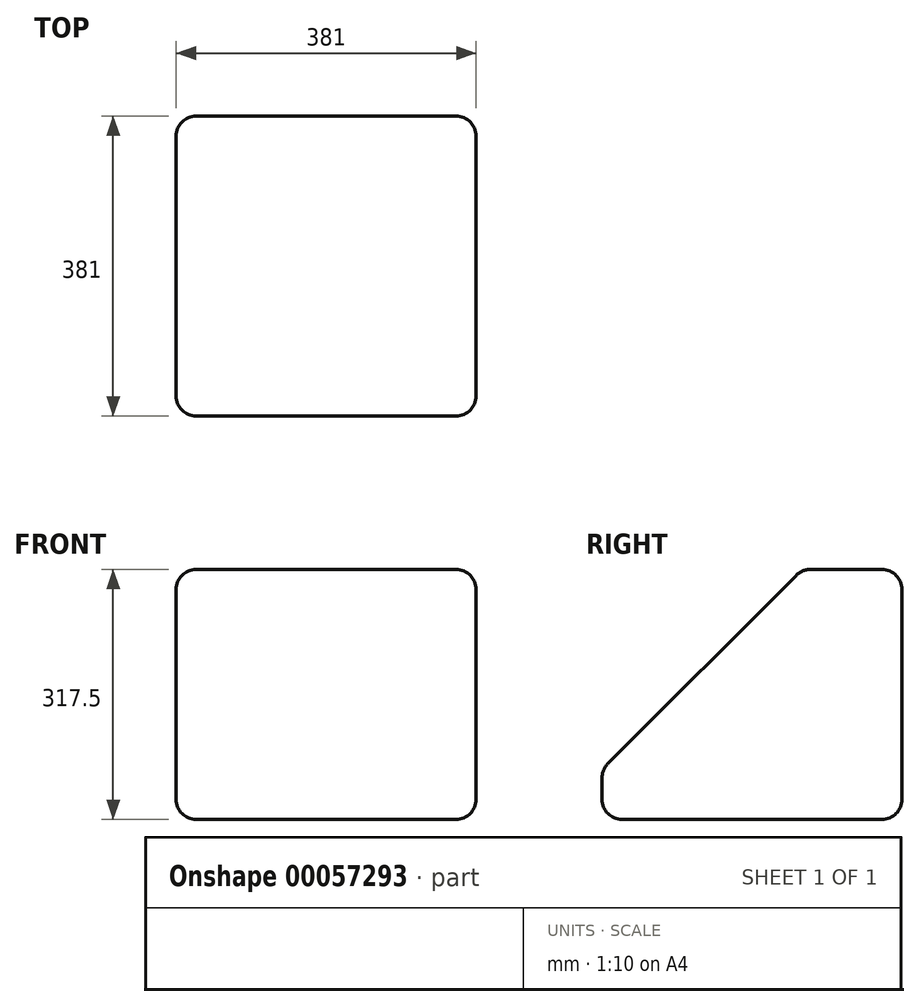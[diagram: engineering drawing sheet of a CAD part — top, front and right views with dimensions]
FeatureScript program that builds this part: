
annotation { "Feature Type Name" : "Feature", "Feature Type Description" : "" }
export const myFeature = defineFeature(function(context is Context, id is Id, definition is map)
    precondition{}
    {
        {
            var Q0;
            Q0=qCreatedBy(makeId("Top.planeOp"),FACE);
            var sketch = newSketch(context, id + "F0", { "sketchPlane" : qUnion([Q0])});
            skLineSegment(sketch, "E0.rect.bottom", {"start": v(190.5, -190.5) * mm, "end": v(-190.5, -190.5) * mm});
            skLineSegment(sketch, "E0.rect.top", {"start": v(190.5, 190.5) * mm, "end": v(-190.5, 190.5) * mm});
            skLineSegment(sketch, "E0.rect.left", {"start": v(190.5, -190.5) * mm, "end": v(190.5, 190.5) * mm});
            skLineSegment(sketch, "E0.rect.right", {"start": v(-190.5, -190.5) * mm, "end": v(-190.5, 190.5) * mm});
            skPoint(sketch, "E0.rect.middle", {"position": v(0, 0) * mm});
            skSolve(sketch);
        }
        {
            var Q0;
            Q0=makeQuery(id+"F0.imprint","IMPRINT",FACE,{"disambiguationData":[TD([[makeQuery(id+"F0.imprint","IMPRINT",EDGE,{"derivedFrom":sQuery(id+"F0.wireOp",EDGE,"E0.rect.bottom")}),-1.0]])]});
            extrude(context, id + "F1", {"entities" : qUnion([Q0]), "depth" : 317.5 * mm});
        }
        {
            var Q0;
            Q0=makeQuery(id+"F1.opExtrude","CAP_EDGE",EDGE,{"disambiguationData":[OSD([sQuery(id+"F0.wireOp",EDGE,"E0.rect.bottom")])],"isStart":false});
            chamfer(context, id + "F2", {"entities" : qUnion([Q0]), "width" : 254 * mm, "tangentPropagation" : true});
        }
        {
            var Q0;
            Q0=makeQuery(id+"F1.opExtrude","SWEPT_FACE",FACE,{"disambiguationData":[OSD([sQuery(id+"F0.wireOp",EDGE,"E0.rect.top")])]});
            var Q1;
            Q1=makeQuery(id+"F1.opExtrude","SWEPT_FACE",FACE,{"disambiguationData":[OSD([sQuery(id+"F0.wireOp",EDGE,"E0.rect.right")])]});
            var Q2;
            Q2=makeQuery(id+"F1.opExtrude","CAP_FACE",FACE,{"disambiguationData":[OSD([sQuery(id+"F0.wireOp",EDGE,"E0.rect.bottom"),sQuery(id+"F0.wireOp",EDGE,"E0.rect.top"),sQuery(id+"F0.wireOp",EDGE,"E0.rect.left"),sQuery(id+"F0.wireOp",EDGE,"E0.rect.right")])],"isStart":false});
            var Q3;
            Q3=makeQuery(id+"F1.opExtrude","SWEPT_FACE",FACE,{"disambiguationData":[OSD([sQuery(id+"F0.wireOp",EDGE,"E0.rect.left")])]});
            var Q4;
            Q4=makeQuery(id+"F1.opExtrude","CAP_FACE",FACE,{"disambiguationData":[OSD([sQuery(id+"F0.wireOp",EDGE,"E0.rect.bottom"),sQuery(id+"F0.wireOp",EDGE,"E0.rect.top"),sQuery(id+"F0.wireOp",EDGE,"E0.rect.left"),sQuery(id+"F0.wireOp",EDGE,"E0.rect.right")])],"isStart":true});
            var Q5;
            Q5=makeQuery(id+"F1.opExtrude","SWEPT_FACE",FACE,{"disambiguationData":[OSD([sQuery(id+"F0.wireOp",EDGE,"E0.rect.bottom")])]});
            fillet(context, id + "F3", {"entities" : qUnion([Q0, Q1, Q2, Q3, Q4, Q5]), "radius" : 25.4 * mm, "tangentPropagation" : true, "allowEdgeOverflow" : false});
        }
    });
